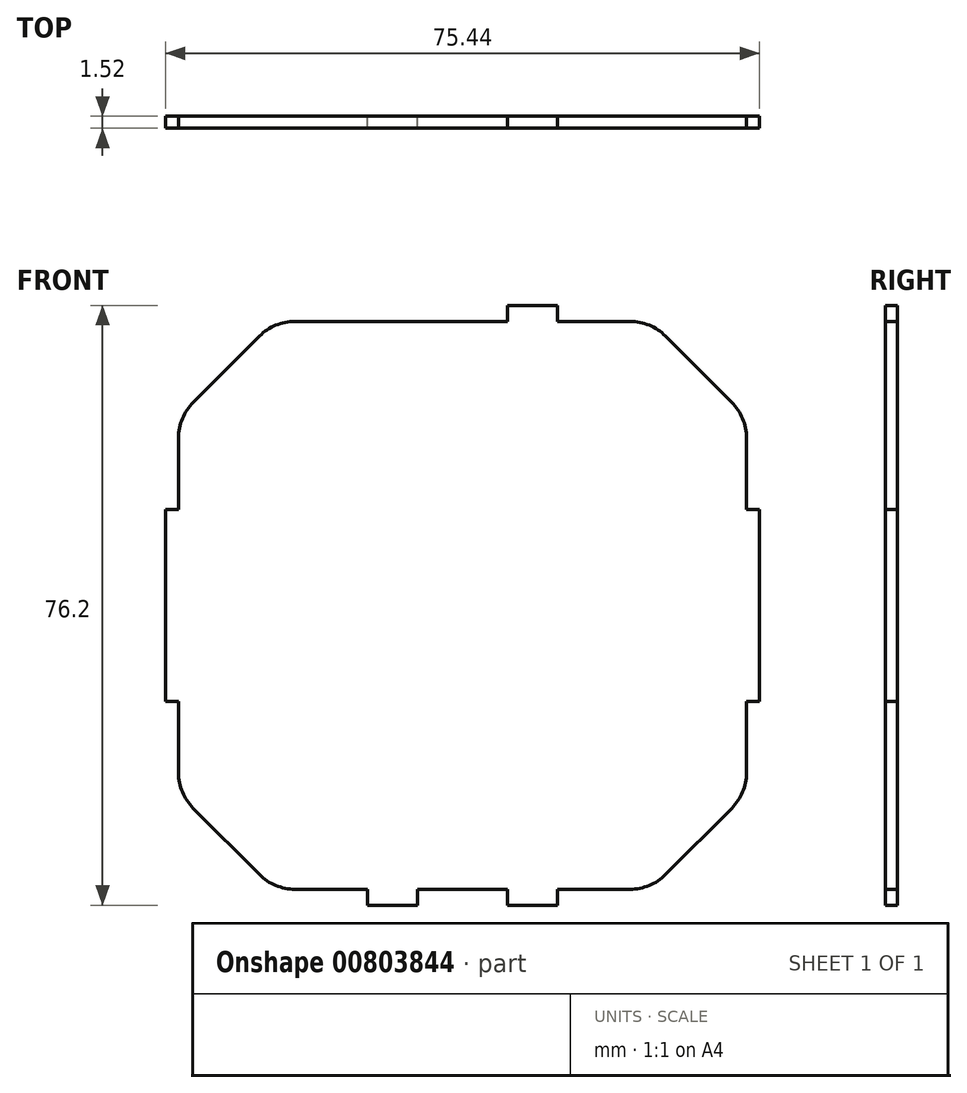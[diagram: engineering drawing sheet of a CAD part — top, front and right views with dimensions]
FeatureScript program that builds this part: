
annotation { "Feature Type Name" : "Feature", "Feature Type Description" : "" }
export const myFeature = defineFeature(function(context is Context, id is Id, definition is map)
    precondition{}
    {
        {
            var Q0;
            Q0=qCreatedBy(makeId("Front.planeOp"),FACE);
            var sketch = newSketch(context, id + "F0", { "sketchPlane" : qUnion([Q0])});
            skLineSegment(sketch, "E0.bottom", {"start": v(21.9, 38.38) * mm, "end": v(-27.63, 38.38) * mm});
            skLineSegment(sketch, "E0.top", {"start": v(21.9, -37.82) * mm, "end": v(-27.63, -37.82) * mm});
            skLineSegment(sketch, "E0.left", {"start": v(35.23, 25.04) * mm, "end": v(35.23, -24.49) * mm});
            skLineSegment(sketch, "E0.right", {"start": v(-40.97, 25.04) * mm, "end": v(-40.97, -24.49) * mm});
            skPoint(sketch, "E0.middle", {"position": v(-2.87, 0.28) * mm});
            skCircle(sketch, "E1.cCircle", {"center": v(-2.87, 0.28) * mm, "radius": 44.45 * mm, "construction": true});
            skLineSegment(sketch, "E1.0", {"start": v(41.58, 18.69) * mm, "end": v(41.58, -18.14) * mm});
            skLineSegment(sketch, "E1.1", {"start": v(35.23, -24.49) * mm, "end": v(21.9, -37.82) * mm});
            skLineSegment(sketch, "E1.2", {"start": v(15.54, -44.17) * mm, "end": v(-21.28, -44.17) * mm});
            skLineSegment(sketch, "E1.3", {"start": v(-27.63, -37.82) * mm, "end": v(-40.97, -24.49) * mm});
            skLineSegment(sketch, "E1.4", {"start": v(-47.32, -18.14) * mm, "end": v(-47.32, 18.69) * mm});
            skLineSegment(sketch, "E1.5", {"start": v(-40.97, 25.04) * mm, "end": v(-27.63, 38.38) * mm});
            skLineSegment(sketch, "E1.6", {"start": v(-21.28, 44.73) * mm, "end": v(15.54, 44.73) * mm});
            skLineSegment(sketch, "E1.7", {"start": v(21.9, 38.38) * mm, "end": v(35.23, 25.04) * mm});
            skPoint(sketch, "E1.0.midPoint", {"position": v(41.58, 0.28) * mm});
            skPoint(sketch, "E2.orphan", {"position": v(-40.97, 38.38) * mm});
            skPoint(sketch, "E3.orphan", {"position": v(-40.97, -37.82) * mm});
            skPoint(sketch, "E4.orphan", {"position": v(35.23, -37.82) * mm});
            skPoint(sketch, "E5.orphan", {"position": v(35.23, 38.38) * mm});
            skLineSegment(sketch, "E6.0", {"start": v(22.9, 34.48) * mm, "end": v(31.34, 26.06) * mm});
            skLineSegment(sketch, "E6.1", {"start": v(33.2, 21.57) * mm, "end": v(33.2, -21.01) * mm});
            skLineSegment(sketch, "E6.2", {"start": v(18.42, 36.34) * mm, "end": v(-24.16, 36.34) * mm});
            skLineSegment(sketch, "E6.3", {"start": v(31.34, -25.5) * mm, "end": v(22.9, -33.93) * mm});
            skLineSegment(sketch, "E6.4", {"start": v(-37.08, 26.06) * mm, "end": v(-28.65, 34.48) * mm});
            skLineSegment(sketch, "E6.5", {"start": v(-38.94, 21.57) * mm, "end": v(-38.94, -21.01) * mm});
            skLineSegment(sketch, "E6.6", {"start": v(-28.65, -33.93) * mm, "end": v(-37.08, -25.5) * mm});
            skLineSegment(sketch, "E6.7", {"start": v(18.42, -35.8) * mm, "end": v(-24.16, -35.8) * mm});
            skPoint(sketch, "E7.visualSharp", {"position": v(-26.8, 36.34) * mm});
            skArc(sketch, "E7.filletArc", {"start": v(-24.16, 36.34) * mm, "mid": v(-26.6, 35.86) * mm, "end": v(-28.65, 34.48) * mm});
            skPoint(sketch, "E8.visualSharp", {"position": v(21.05, 36.34) * mm});
            skArc(sketch, "E8.filletArc", {"start": v(22.9, 34.48) * mm, "mid": v(20.85, 35.86) * mm, "end": v(18.42, 36.34) * mm});
            skPoint(sketch, "E9.visualSharp", {"position": v(33.2, 24.2) * mm});
            skArc(sketch, "E9.filletArc", {"start": v(33.2, 21.57) * mm, "mid": v(32.71, 24) * mm, "end": v(31.34, 26.06) * mm});
            skPoint(sketch, "E10.visualSharp", {"position": v(33.2, -23.64) * mm});
            skArc(sketch, "E10.filletArc", {"start": v(31.34, -25.5) * mm, "mid": v(32.71, -23.44) * mm, "end": v(33.2, -21.01) * mm});
            skPoint(sketch, "E11.visualSharp", {"position": v(21.05, -35.8) * mm});
            skArc(sketch, "E11.filletArc", {"start": v(18.42, -35.8) * mm, "mid": v(20.85, -35.3) * mm, "end": v(22.9, -33.93) * mm});
            skPoint(sketch, "E12.visualSharp", {"position": v(-26.8, -35.8) * mm});
            skArc(sketch, "E12.filletArc", {"start": v(-28.65, -33.93) * mm, "mid": v(-26.6, -35.3) * mm, "end": v(-24.16, -35.8) * mm});
            skPoint(sketch, "E13.visualSharp", {"position": v(-38.94, -23.64) * mm});
            skArc(sketch, "E13.filletArc", {"start": v(-38.94, -21.01) * mm, "mid": v(-38.46, -23.44) * mm, "end": v(-37.08, -25.5) * mm});
            skPoint(sketch, "E14.visualSharp", {"position": v(-38.94, 24.2) * mm});
            skArc(sketch, "E14.filletArc", {"start": v(-37.08, 26.06) * mm, "mid": v(-38.46, 24) * mm, "end": v(-38.94, 21.57) * mm});
            skLineSegment(sketch, "E15.bottom", {"start": v(-14.93, 38.38) * mm, "end": v(-8.58, 38.38) * mm});
            skLineSegment(sketch, "E15.top", {"start": v(-14.93, 36.34) * mm, "end": v(-8.58, 36.34) * mm});
            skLineSegment(sketch, "E15.left", {"start": v(-14.93, 38.38) * mm, "end": v(-14.93, 36.34) * mm});
            skLineSegment(sketch, "E15.right", {"start": v(-8.58, 38.38) * mm, "end": v(-8.58, 36.34) * mm});
            skPoint(sketch, "E16", {"position": v(-11.76, 38.38) * mm});
            skLineSegment(sketch, "E17", {"start": v(-2.87, 36.34) * mm, "end": v(-2.87, -35.8) * mm, "construction": true});
            skLineSegment(sketch, "E18", {"start": v(-38.94, 0.28) * mm, "end": v(33.2, 0.28) * mm, "construction": true});
            skLineSegment(sketch, "E19.MirrorCS", {"start": v(33.2, 0.28) * mm, "end": v(-38.94, 0.28) * mm, "construction": true});
            skLineSegment(sketch, "E20.MirrorCS", {"start": v(9.2, 38.38) * mm, "end": v(9.2, 36.34) * mm});
            skPoint(sketch, "E21.MirrorP", {"position": v(6.02, 38.38) * mm});
            skLineSegment(sketch, "E22.MirrorCS", {"start": v(9.2, 36.34) * mm, "end": v(2.84, 36.34) * mm});
            skLineSegment(sketch, "E23.MirrorCS", {"start": v(2.84, 38.38) * mm, "end": v(2.84, 36.34) * mm});
            skLineSegment(sketch, "E24.MirrorCS", {"start": v(9.2, 38.38) * mm, "end": v(2.84, 38.38) * mm});
            skLineSegment(sketch, "E25.MirrorCS", {"start": v(-14.93, -37.82) * mm, "end": v(-14.93, -35.8) * mm});
            skLineSegment(sketch, "E26.MirrorCS", {"start": v(-8.58, -37.82) * mm, "end": v(-8.58, -35.8) * mm});
            skPoint(sketch, "E27.MirrorP", {"position": v(-11.76, -37.82) * mm});
            skLineSegment(sketch, "E28.MirrorCS", {"start": v(-14.93, -35.8) * mm, "end": v(-8.58, -35.8) * mm});
            skLineSegment(sketch, "E29.MirrorCS", {"start": v(-14.93, -37.82) * mm, "end": v(-8.58, -37.82) * mm});
            skLineSegment(sketch, "E30.MirrorCS", {"start": v(2.84, -37.82) * mm, "end": v(2.84, -35.8) * mm});
            skLineSegment(sketch, "E31.MirrorCS", {"start": v(9.2, -35.8) * mm, "end": v(2.84, -35.8) * mm});
            skPoint(sketch, "E32.MirrorP", {"position": v(6.02, -37.82) * mm});
            skLineSegment(sketch, "E33.MirrorCS", {"start": v(9.2, -37.82) * mm, "end": v(9.2, -35.8) * mm});
            skLineSegment(sketch, "E34.MirrorCS", {"start": v(9.2, -37.82) * mm, "end": v(2.84, -37.82) * mm});
            skLineSegment(sketch, "E35.0", {"start": v(-38.94, -11.92) * mm, "end": v(35.23, -11.92) * mm});
            skLineSegment(sketch, "E36.0", {"start": v(-38.94, 12.47) * mm, "end": v(35.23, 12.47) * mm});
            skLineSegment(sketch, "E37.MirrorCS", {"start": v(33.2, 12.47) * mm, "end": v(-40.97, 12.47) * mm});
            skLineSegment(sketch, "E38.MirrorCS", {"start": v(33.2, -11.92) * mm, "end": v(-40.97, -11.92) * mm});
            skLineSegment(sketch, "E39.0", {"start": v(34.85, 25.04) * mm, "end": v(34.85, -24.49) * mm});
            skLineSegment(sketch, "E40.0", {"start": v(-40.6, 25.04) * mm, "end": v(-40.6, -24.49) * mm});
            skSolve(sketch);
        }
        {
            var Q0;
            Q0=makeQuery(id+"F0.imprint","IMPRINT",FACE,{"disambiguationData":[TD([[makeQuery(id+"F0.imprint","IMPRINT",EDGE,{"derivedFrom":sQuery(id+"F0.wireOp",EDGE,"E6.0")}),-1.0]])]});
            var Q1;
            Q1=makeQuery(id+"F0.imprint","IMPRINT",FACE,{"disambiguationData":[TD([[makeQuery(id+"F0.imprint","IMPRINT",EDGE,{"derivedFrom":sQuery(id+"F0.wireOp",EDGE,"E15.bottom")}),-1.0]])]});
            var Q2;
            Q2=makeQuery(id+"F0.imprint","IMPRINT",FACE,{"disambiguationData":[TD([[makeQuery(id+"F0.imprint","IMPRINT",EDGE,{"derivedFrom":sQuery(id+"F0.wireOp",EDGE,"E20.MirrorCS")}),-1.0]])]});
            var Q3;
            Q3=makeQuery(id+"F0.imprint","IMPRINT",FACE,{"disambiguationData":[TD([[makeQuery(id+"F0.imprint","IMPRINT",EDGE,{"derivedFrom":sQuery(id+"F0.wireOp",EDGE,"E25.MirrorCS")}),-1.0]])]});
            var Q4;
            Q4=makeQuery(id+"F0.imprint","IMPRINT",FACE,{"disambiguationData":[TD([[makeQuery(id+"F0.imprint","IMPRINT",EDGE,{"derivedFrom":sQuery(id+"F0.wireOp",EDGE,"E30.MirrorCS")}),-1.0]])]});
            var Q5;
            Q5=makeQuery(id+"F0.imprint","IMPRINT",FACE,{"disambiguationData":[TD([[makeQuery(id+"F0.imprint","IMPRINT",EDGE,{"derivedFrom":sQuery(id+"F0.wireOp",EDGE,"E6.3")}),-1.0]])]});
            var Q6;
            {var subQ3=sQuery(id+"F0.wireOp",EDGE,"E37.MirrorCS");var subQ5=sQuery(id+"F0.wireOp",EDGE,"E6.5");var subQ6=makeQuery(id+"F0.imprint","INTERSECT",VERTEX,{"derivedFrom":[subQ5,subQ3]});Q6=makeQuery(id+"F0.imprint","IMPRINT",FACE,{"disambiguationData":[TD([[makeQuery(id+"F0.imprint","IMPRINT",EDGE,{"disambiguationData":[TD([[subQ6,-1.0]])],"derivedFrom":subQ5}),1.0]])]});}
            var Q7;
            {var subQ0=sQuery(id+"F0.wireOp",EDGE,"E37.MirrorCS");var subQ1=sQuery(id+"F0.wireOp",EDGE,"E6.5");var subQ2=makeQuery(id+"F0.imprint","INTERSECT",VERTEX,{"derivedFrom":[subQ1,subQ0]});Q7=makeQuery(id+"F0.imprint","IMPRINT",FACE,{"disambiguationData":[TD([[makeQuery(id+"F0.imprint","IMPRINT",EDGE,{"disambiguationData":[TD([[subQ2,-1.0]])],"derivedFrom":subQ1}),-1.0]])]});}
            var Q8;
            {var subQ0=sQuery(id+"F0.wireOp",EDGE,"E35.0");var subQ5=sQuery(id+"F0.wireOp",EDGE,"E39.0");var subQ7=makeQuery(id+"F0.imprint","INTERSECT",VERTEX,{"derivedFrom":[subQ0,subQ5]});Q8=makeQuery(id+"F0.imprint","IMPRINT",FACE,{"disambiguationData":[TD([[makeQuery(id+"F0.imprint","IMPRINT",EDGE,{"disambiguationData":[TD([[subQ7,1.0]])],"derivedFrom":subQ5}),-1.0]])]});}
            extrude(context, id + "F1", {"entities" : qUnion([Q0, Q1, Q2, Q3, Q4, Q5, Q6, Q7, Q8]), "depth" : 1.52 * mm, "offsetDistance" : 25.4 * mm});
        }
    });
